# Revit family: WaterConditioner_ION_SB100-SB200
name_source: partatom
category: Mechanical Equipment
revit_build: Autodesk Revit 2014 (Build: 20130308_1515(x64)
units: mm (PartAtom-declared; Revit-internal decimal feet)

## types (4) — shared parameters
Assembly Code = D2020300
Density_Water_20_ION = 998.2000 kg/m³
Issue_Date_ION = 01/07/15
Issue_Rev_ION = A
Manufacturer = ION Enterprises
URL = www.scalebuster.com
UnitConvert_Area = 1 m²

## per-type parameters (varying)
| type | Equipment_Dia_ION | Equipment_Length_ION | FlangeSize | Model | UnitConvert_PressureFactor | UnitSize | Water_ConnectionDia_ION | Weight_Dry_ION |
| DN100 | 178 mm | 445 mm  [stored 1.45997 ft] | Flange_PN16_8Hole : DN100 | SB100 | 74522 | FlangeBody_100-200 : DN100 | 100 mm | 32.00 kg |
| DN125 | 200 mm  [stored 0.656168 ft] | 445 mm  [stored 1.45997 ft] | Flange_PN16_8Hole : DN125 | SB125 | 41914 | FlangeBody_100-200 : DN125 | 125 mm | 50.00 kg |
| DN150 | 250 mm  [stored 0.82021 ft] | 520 mm  [stored 1.70604 ft] | Flange_PN16_8Hole : DN150 | SB150 | 4830 | FlangeBody_100-200 : DN150 | 150 mm | 80.00 kg |
| DN200 | 308 mm  [stored 1.0105 ft] | 520 mm  [stored 1.70604 ft] | Flange_PN16_8Hole : DN200 | SB200 | 1525 | FlangeBody_100-200 : DN200 | 200 mm | 120.00 kg |

note: [stored X ft] marks values corroborated as IEEE doubles in the binary element streams (Revit-internal decimal feet)

## geometry (parser evidence)
native form markers: Sweep x6
no freeform markers — native parametric forms only
